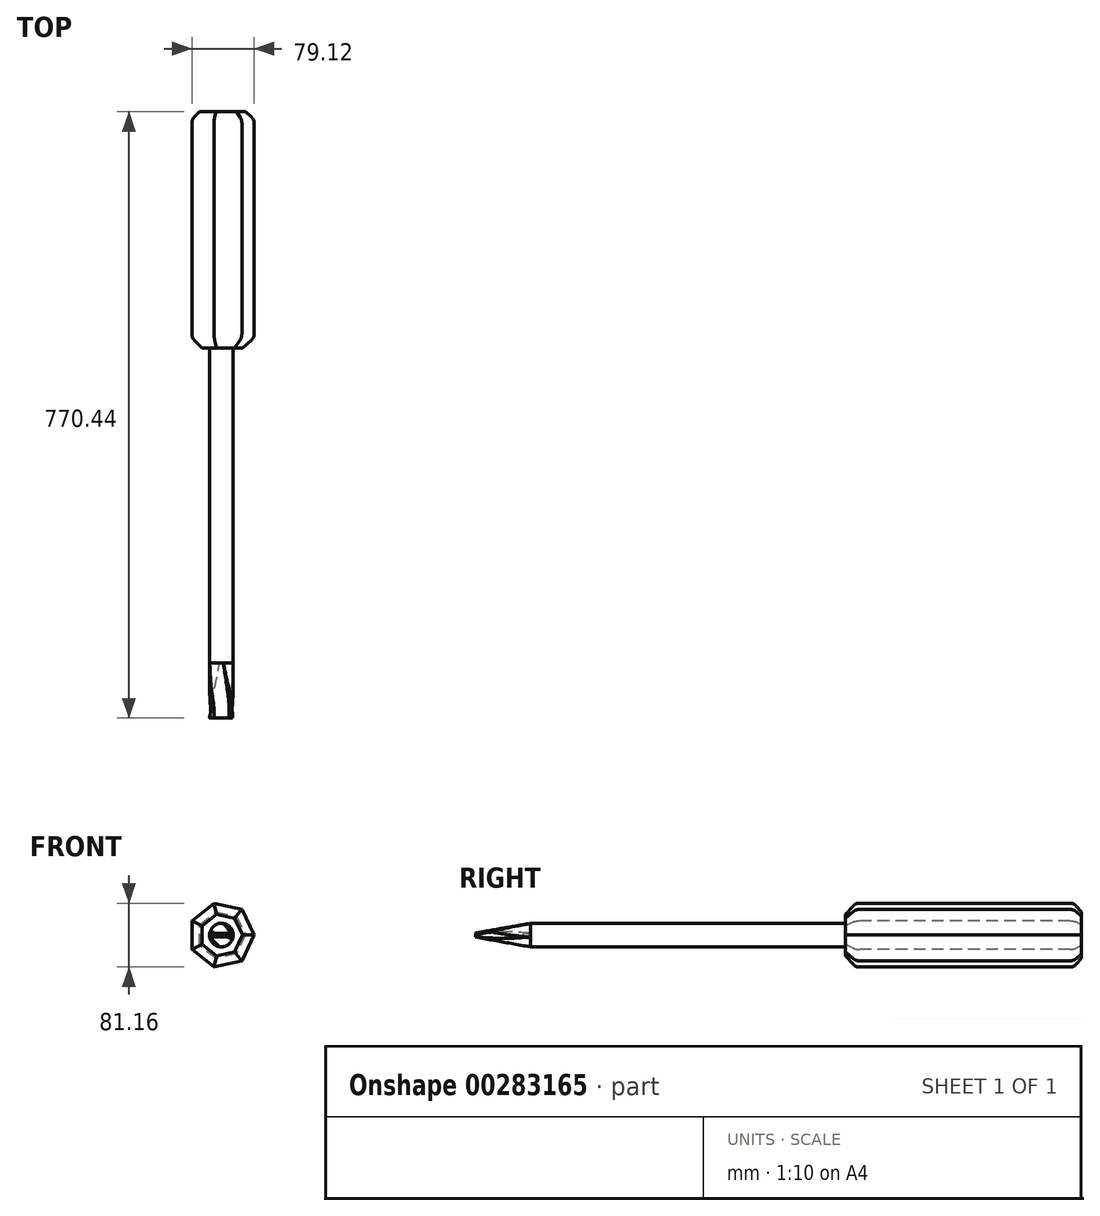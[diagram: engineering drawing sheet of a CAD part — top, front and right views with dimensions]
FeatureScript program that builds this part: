
annotation { "Feature Type Name" : "Feature", "Feature Type Description" : "" }
export const myFeature = defineFeature(function(context is Context, id is Id, definition is map)
    precondition{}
    {
        {
            var Q0;
            Q0=qCreatedBy(makeId("Front.planeOp"),FACE);
            var sketch = newSketch(context, id + "F0", { "sketchPlane" : qUnion([Q0])});
            skCircle(sketch, "E0", {"center": v(0, 0) * mm, "radius": 15 * mm});
            skSolve(sketch);
        }
        {
            var Q0;
            Q0=qCreatedBy(makeId("Front.planeOp"),FACE);
            cPlane(context, id + "F1", {"entities" : qUnion([Q0]), "cplaneType" : CPlaneType.OFFSET, "offset" : 70 * mm, "width" : 150 * mm, "height" : 150 * mm});
        }
        {
            var Q0;
            Q0=qCreatedBy(id+"F1.planeOp",FACE);
            var sketch = newSketch(context, id + "F2", { "sketchPlane" : qUnion([Q0])});
            skLineSegment(sketch, "E1.bottom", {"start": v(15, -2.5) * mm, "end": v(-15, -2.5) * mm});
            skLineSegment(sketch, "E1.top", {"start": v(15, 2.5) * mm, "end": v(-15, 2.5) * mm});
            skLineSegment(sketch, "E1.left", {"start": v(15, -2.5) * mm, "end": v(15, 2.5) * mm});
            skLineSegment(sketch, "E1.right", {"start": v(-15, -2.5) * mm, "end": v(-15, 2.5) * mm});
            skPoint(sketch, "E1.middle", {"position": v(0, 0) * mm});
            skSolve(sketch);
        }
        {
            var Q0;
            Q0=makeQuery(id+"F2.imprint","IMPRINT",FACE,{"disambiguationData":[TD([[makeQuery(id+"F2.imprint","IMPRINT",EDGE,{"derivedFrom":sQuery(id+"F2.wireOp",EDGE,"E1.bottom")}),-1.0]])]});
            var Q1;
            Q1=makeQuery(id+"F0.imprint","IMPRINT",FACE,{"disambiguationData":[TD([[makeQuery(id+"F0.imprint","IMPRINT",EDGE,{"derivedFrom":sQuery(id+"F0.wireOp",EDGE,"E0")}),1.0]])]});
            loft(context, id + "F3", {"sheetProfilesArray" : [{ "sheetProfileEntities" : qUnion([Q0]) }, { "sheetProfileEntities" : qUnion([Q1]) }]});
        }
        {
            var Q0;
            Q0=makeQuery(id+"F3.opLoft","CAP_FACE",FACE,{"disambiguationData":[OSD([makeQuery(id+"F0.imprint","IMPRINT",FACE,{"disambiguationData":[TD([[makeQuery(id+"F0.imprint","IMPRINT",EDGE,{"derivedFrom":sQuery(id+"F0.wireOp",EDGE,"E0")}),1.0]])]})])],"isStart":true});
            extrude(context, id + "F4", {"entities" : qUnion([Q0]), "operationType" : NewBodyOperationType.ADD, "depth" : 400 * mm});
        }
        {
            var Q0;
            Q0=makeQuery(id+"F3.opLoft","SWEPT_EDGE",EDGE,{"disambiguationData":[OSD([sQuery(id+"F0.wireOp",EDGE,"E0"),sQuery(id+"F2.wireOp",EDGE,"E1.top"),sQuery(id+"F2.wireOp",EDGE,"E1.left"),sQuery(id+"F2.wireOp",EDGE,"E1.right")])]});
            var Q1;
            Q1=makeQuery(id+"F3.opLoft","SWEPT_EDGE",EDGE,{"disambiguationData":[OSD([sQuery(id+"F0.wireOp",EDGE,"E0"),sQuery(id+"F2.wireOp",EDGE,"E1.bottom"),sQuery(id+"F2.wireOp",EDGE,"E1.top"),sQuery(id+"F2.wireOp",EDGE,"E1.right")])]});
            var Q2;
            Q2=makeQuery(id+"F3.opLoft","SWEPT_EDGE",EDGE,{"disambiguationData":[OSD([sQuery(id+"F0.wireOp",EDGE,"E0"),sQuery(id+"F2.wireOp",EDGE,"E1.bottom"),sQuery(id+"F2.wireOp",EDGE,"E1.left"),sQuery(id+"F2.wireOp",EDGE,"E1.right")])]});
            var Q3;
            Q3=makeQuery(id+"F3.opLoft","SWEPT_EDGE",EDGE,{"disambiguationData":[OSD([sQuery(id+"F2.wireOp",EDGE,"E1.bottom"),sQuery(id+"F2.wireOp",EDGE,"E1.left")])]});
            fillet(context, id + "F5", {"entities" : qUnion([Q0, Q1, Q2, Q3]), "radius" : 5 * mm, "tangentPropagation" : true, "allowEdgeOverflow" : false});
        }
        {
            var Q0;
            Q0=qCreatedBy(makeId("Front.planeOp"),FACE);
            cPlane(context, id + "F6", {"entities" : qUnion([Q0]), "cplaneType" : CPlaneType.OFFSET, "offset" : 400 * mm, "oppositeDirection" : true, "width" : 150 * mm, "height" : 150 * mm});
        }
        {
            var Q0;
            Q0=qCreatedBy(id+"F6.planeOp",FACE);
            var sketch = newSketch(context, id + "F7", { "sketchPlane" : qUnion([Q0])});
            skCircle(sketch, "E2.cCircle", {"center": v(0, 0) * mm, "radius": 37.5 * mm, "construction": true});
            skLineSegment(sketch, "E2.0", {"start": v(-37.5, -18.06) * mm, "end": v(-37.5, 18.06) * mm});
            skLineSegment(sketch, "E2.1", {"start": v(-37.5, 18.06) * mm, "end": v(-9.26, 40.58) * mm});
            skLineSegment(sketch, "E2.2", {"start": v(-9.26, 40.58) * mm, "end": v(25.95, 32.54) * mm});
            skLineSegment(sketch, "E2.3", {"start": v(25.95, 32.54) * mm, "end": v(41.62, 0) * mm});
            skLineSegment(sketch, "E2.4", {"start": v(41.62, 0) * mm, "end": v(25.95, -32.54) * mm});
            skLineSegment(sketch, "E2.5", {"start": v(25.95, -32.54) * mm, "end": v(-9.26, -40.58) * mm});
            skLineSegment(sketch, "E2.6", {"start": v(-9.26, -40.58) * mm, "end": v(-37.5, -18.06) * mm});
            skPoint(sketch, "E2.0.midPoint", {"position": v(-37.5, 0) * mm});
            skSolve(sketch);
        }
        {
            var Q0;
            Q0 = qSketchRegion(id + "F7", true);
            extrude(context, id + "F8", {"entities" : qUnion([Q0]), "operationType" : NewBodyOperationType.ADD, "oppositeDirection" : true, "depth" : 300 * mm});
        }
        {
            var Q0;
            Q0=makeQuery(id+"F8.opExtrude","CAP_EDGE",EDGE,{"disambiguationData":[OSD([sQuery(id+"F7.wireOp",EDGE,"E2.2")])],"isStart":true});
            var Q1;
            Q1=makeQuery(id+"F8.opExtrude","CAP_EDGE",EDGE,{"disambiguationData":[OSD([sQuery(id+"F7.wireOp",EDGE,"E2.3")])],"isStart":true});
            var Q2;
            Q2=makeQuery(id+"F8.opExtrude","CAP_EDGE",EDGE,{"disambiguationData":[OSD([sQuery(id+"F7.wireOp",EDGE,"E2.4")])],"isStart":true});
            var Q3;
            Q3=makeQuery(id+"F8.opExtrude","CAP_EDGE",EDGE,{"disambiguationData":[OSD([sQuery(id+"F7.wireOp",EDGE,"E2.5")])],"isStart":true});
            var Q4;
            Q4=makeQuery(id+"F8.opExtrude","CAP_EDGE",EDGE,{"disambiguationData":[OSD([sQuery(id+"F7.wireOp",EDGE,"E2.1")])],"isStart":true});
            var Q5;
            Q5=makeQuery(id+"F8.opExtrude","CAP_EDGE",EDGE,{"disambiguationData":[OSD([sQuery(id+"F7.wireOp",EDGE,"E2.0")])],"isStart":true});
            var Q6;
            Q6=makeQuery(id+"F8.opExtrude","CAP_EDGE",EDGE,{"disambiguationData":[OSD([sQuery(id+"F7.wireOp",EDGE,"E2.6")])],"isStart":true});
            chamfer(context, id + "F9", {"entities" : qUnion([Q0, Q1, Q2, Q3, Q4, Q5, Q6]), "width" : 13 * mm, "tangentPropagation" : true});
        }
        {
            var Q0;
            {var subQ0=sQuery(id+"F7.wireOp",EDGE,"E2.3");Q0=makeQuery(id+"F9.opChamfer","BLEND_EDGE",EDGE,{"blendedFrom":[makeQuery(id+"F8.opExtrude","CAP_EDGE",EDGE,{"disambiguationData":[OSD([subQ0])],"isStart":true}),makeQuery(id+"F8.opExtrude","SWEPT_FACE",FACE,{"disambiguationData":[OSD([subQ0])]})],"blendedInto":[makeQuery(id+"F8.opExtrude","SWEPT_FACE",FACE,{"disambiguationData":[OSD([subQ0])]})]});}
            var Q1;
            {var subQ0=sQuery(id+"F7.wireOp",EDGE,"E2.2");Q1=makeQuery(id+"F9.opChamfer","BLEND_EDGE",EDGE,{"blendedFrom":[makeQuery(id+"F8.opExtrude","CAP_EDGE",EDGE,{"disambiguationData":[OSD([subQ0])],"isStart":true}),makeQuery(id+"F8.opExtrude","SWEPT_FACE",FACE,{"disambiguationData":[OSD([subQ0])]})],"blendedInto":[makeQuery(id+"F8.opExtrude","SWEPT_FACE",FACE,{"disambiguationData":[OSD([subQ0])]})]});}
            var Q2;
            {var subQ0=sQuery(id+"F7.wireOp",EDGE,"E2.1");Q2=makeQuery(id+"F9.opChamfer","BLEND_EDGE",EDGE,{"blendedFrom":[makeQuery(id+"F8.opExtrude","CAP_EDGE",EDGE,{"disambiguationData":[OSD([subQ0])],"isStart":true}),makeQuery(id+"F8.opExtrude","SWEPT_FACE",FACE,{"disambiguationData":[OSD([subQ0])]})],"blendedInto":[makeQuery(id+"F8.opExtrude","SWEPT_FACE",FACE,{"disambiguationData":[OSD([subQ0])]})]});}
            var Q3;
            {var subQ0=sQuery(id+"F7.wireOp",EDGE,"E2.0");Q3=makeQuery(id+"F9.opChamfer","BLEND_EDGE",EDGE,{"blendedFrom":[makeQuery(id+"F8.opExtrude","CAP_EDGE",EDGE,{"disambiguationData":[OSD([subQ0])],"isStart":true}),makeQuery(id+"F8.opExtrude","SWEPT_FACE",FACE,{"disambiguationData":[OSD([subQ0])]})],"blendedInto":[makeQuery(id+"F8.opExtrude","SWEPT_FACE",FACE,{"disambiguationData":[OSD([subQ0])]})]});}
            var Q4;
            {var subQ0=sQuery(id+"F7.wireOp",EDGE,"E2.4");Q4=makeQuery(id+"F9.opChamfer","BLEND_EDGE",EDGE,{"blendedFrom":[makeQuery(id+"F8.opExtrude","CAP_EDGE",EDGE,{"disambiguationData":[OSD([subQ0])],"isStart":true}),makeQuery(id+"F8.opExtrude","SWEPT_FACE",FACE,{"disambiguationData":[OSD([subQ0])]})],"blendedInto":[makeQuery(id+"F8.opExtrude","SWEPT_FACE",FACE,{"disambiguationData":[OSD([subQ0])]})]});}
            var Q5;
            {var subQ0=sQuery(id+"F7.wireOp",EDGE,"E2.5");Q5=makeQuery(id+"F9.opChamfer","BLEND_EDGE",EDGE,{"blendedFrom":[makeQuery(id+"F8.opExtrude","CAP_EDGE",EDGE,{"disambiguationData":[OSD([subQ0])],"isStart":true}),makeQuery(id+"F8.opExtrude","SWEPT_FACE",FACE,{"disambiguationData":[OSD([subQ0])]})],"blendedInto":[makeQuery(id+"F8.opExtrude","SWEPT_FACE",FACE,{"disambiguationData":[OSD([subQ0])]})]});}
            var Q6;
            {var subQ0=sQuery(id+"F7.wireOp",EDGE,"E2.6");Q6=makeQuery(id+"F9.opChamfer","BLEND_EDGE",EDGE,{"blendedFrom":[makeQuery(id+"F8.opExtrude","CAP_EDGE",EDGE,{"disambiguationData":[OSD([subQ0])],"isStart":true}),makeQuery(id+"F8.opExtrude","SWEPT_FACE",FACE,{"disambiguationData":[OSD([subQ0])]})],"blendedInto":[makeQuery(id+"F8.opExtrude","SWEPT_FACE",FACE,{"disambiguationData":[OSD([subQ0])]})]});}
            fillet(context, id + "F10", {"entities" : qUnion([Q0, Q1, Q2, Q3, Q4, Q5, Q6]), "radius" : 10 * mm, "tangentPropagation" : true, "allowEdgeOverflow" : false});
        }
        {
            var Q0;
            Q0=makeQuery(id+"F8.opExtrude","CAP_EDGE",EDGE,{"disambiguationData":[OSD([sQuery(id+"F7.wireOp",EDGE,"E2.4")])],"isStart":false});
            var Q1;
            Q1=makeQuery(id+"F8.opExtrude","CAP_EDGE",EDGE,{"disambiguationData":[OSD([sQuery(id+"F7.wireOp",EDGE,"E2.5")])],"isStart":false});
            var Q2;
            Q2=makeQuery(id+"F8.opExtrude","CAP_EDGE",EDGE,{"disambiguationData":[OSD([sQuery(id+"F7.wireOp",EDGE,"E2.6")])],"isStart":false});
            var Q3;
            Q3=makeQuery(id+"F8.opExtrude","CAP_EDGE",EDGE,{"disambiguationData":[OSD([sQuery(id+"F7.wireOp",EDGE,"E2.0")])],"isStart":false});
            var Q4;
            Q4=makeQuery(id+"F8.opExtrude","CAP_EDGE",EDGE,{"disambiguationData":[OSD([sQuery(id+"F7.wireOp",EDGE,"E2.1")])],"isStart":false});
            var Q5;
            Q5=makeQuery(id+"F8.opExtrude","CAP_EDGE",EDGE,{"disambiguationData":[OSD([sQuery(id+"F7.wireOp",EDGE,"E2.2")])],"isStart":false});
            var Q6;
            Q6=makeQuery(id+"F8.opExtrude","CAP_EDGE",EDGE,{"disambiguationData":[OSD([sQuery(id+"F7.wireOp",EDGE,"E2.3")])],"isStart":false});
            chamfer(context, id + "F11", {"entities" : qUnion([Q0, Q1, Q2, Q3, Q4, Q5, Q6]), "width" : 10 * mm, "tangentPropagation" : true});
        }
        {
            var Q0;
            {var subQ0=sQuery(id+"F7.wireOp",EDGE,"E2.3");Q0=makeQuery(id+"F11.opChamfer","BLEND_EDGE",EDGE,{"blendedFrom":[makeQuery(id+"F8.opExtrude","CAP_EDGE",EDGE,{"disambiguationData":[OSD([subQ0])],"isStart":false}),makeQuery(id+"F8.opExtrude","SWEPT_FACE",FACE,{"disambiguationData":[OSD([subQ0])]})],"blendedInto":[makeQuery(id+"F8.opExtrude","SWEPT_FACE",FACE,{"disambiguationData":[OSD([subQ0])]})]});}
            var Q1;
            {var subQ0=sQuery(id+"F7.wireOp",EDGE,"E2.4");Q1=makeQuery(id+"F11.opChamfer","BLEND_EDGE",EDGE,{"blendedFrom":[makeQuery(id+"F8.opExtrude","CAP_EDGE",EDGE,{"disambiguationData":[OSD([subQ0])],"isStart":false}),makeQuery(id+"F8.opExtrude","SWEPT_FACE",FACE,{"disambiguationData":[OSD([subQ0])]})],"blendedInto":[makeQuery(id+"F8.opExtrude","SWEPT_FACE",FACE,{"disambiguationData":[OSD([subQ0])]})]});}
            var Q2;
            {var subQ0=sQuery(id+"F7.wireOp",EDGE,"E2.5");Q2=makeQuery(id+"F11.opChamfer","BLEND_EDGE",EDGE,{"blendedFrom":[makeQuery(id+"F8.opExtrude","CAP_EDGE",EDGE,{"disambiguationData":[OSD([subQ0])],"isStart":false}),makeQuery(id+"F8.opExtrude","SWEPT_FACE",FACE,{"disambiguationData":[OSD([subQ0])]})],"blendedInto":[makeQuery(id+"F8.opExtrude","SWEPT_FACE",FACE,{"disambiguationData":[OSD([subQ0])]})]});}
            var Q3;
            {var subQ0=sQuery(id+"F7.wireOp",EDGE,"E2.6");Q3=makeQuery(id+"F11.opChamfer","BLEND_EDGE",EDGE,{"blendedFrom":[makeQuery(id+"F8.opExtrude","CAP_EDGE",EDGE,{"disambiguationData":[OSD([subQ0])],"isStart":false}),makeQuery(id+"F8.opExtrude","SWEPT_FACE",FACE,{"disambiguationData":[OSD([subQ0])]})],"blendedInto":[makeQuery(id+"F8.opExtrude","SWEPT_FACE",FACE,{"disambiguationData":[OSD([subQ0])]})]});}
            var Q4;
            {var subQ0=sQuery(id+"F7.wireOp",EDGE,"E2.0");Q4=makeQuery(id+"F11.opChamfer","BLEND_EDGE",EDGE,{"blendedFrom":[makeQuery(id+"F8.opExtrude","CAP_EDGE",EDGE,{"disambiguationData":[OSD([subQ0])],"isStart":false}),makeQuery(id+"F8.opExtrude","SWEPT_FACE",FACE,{"disambiguationData":[OSD([subQ0])]})],"blendedInto":[makeQuery(id+"F8.opExtrude","SWEPT_FACE",FACE,{"disambiguationData":[OSD([subQ0])]})]});}
            var Q5;
            {var subQ0=sQuery(id+"F7.wireOp",EDGE,"E2.1");Q5=makeQuery(id+"F11.opChamfer","BLEND_EDGE",EDGE,{"blendedFrom":[makeQuery(id+"F8.opExtrude","CAP_EDGE",EDGE,{"disambiguationData":[OSD([subQ0])],"isStart":false}),makeQuery(id+"F8.opExtrude","SWEPT_FACE",FACE,{"disambiguationData":[OSD([subQ0])]})],"blendedInto":[makeQuery(id+"F8.opExtrude","SWEPT_FACE",FACE,{"disambiguationData":[OSD([subQ0])]})]});}
            var Q6;
            {var subQ0=sQuery(id+"F7.wireOp",EDGE,"E2.2");Q6=makeQuery(id+"F11.opChamfer","BLEND_EDGE",EDGE,{"blendedFrom":[makeQuery(id+"F8.opExtrude","CAP_EDGE",EDGE,{"disambiguationData":[OSD([subQ0])],"isStart":false}),makeQuery(id+"F8.opExtrude","SWEPT_FACE",FACE,{"disambiguationData":[OSD([subQ0])]})],"blendedInto":[makeQuery(id+"F8.opExtrude","SWEPT_FACE",FACE,{"disambiguationData":[OSD([subQ0])]})]});}
            fillet(context, id + "F12", {"entities" : qUnion([Q0, Q1, Q2, Q3, Q4, Q5, Q6]), "radius" : 10 * mm, "tangentPropagation" : true, "allowEdgeOverflow" : false});
        }
    });
